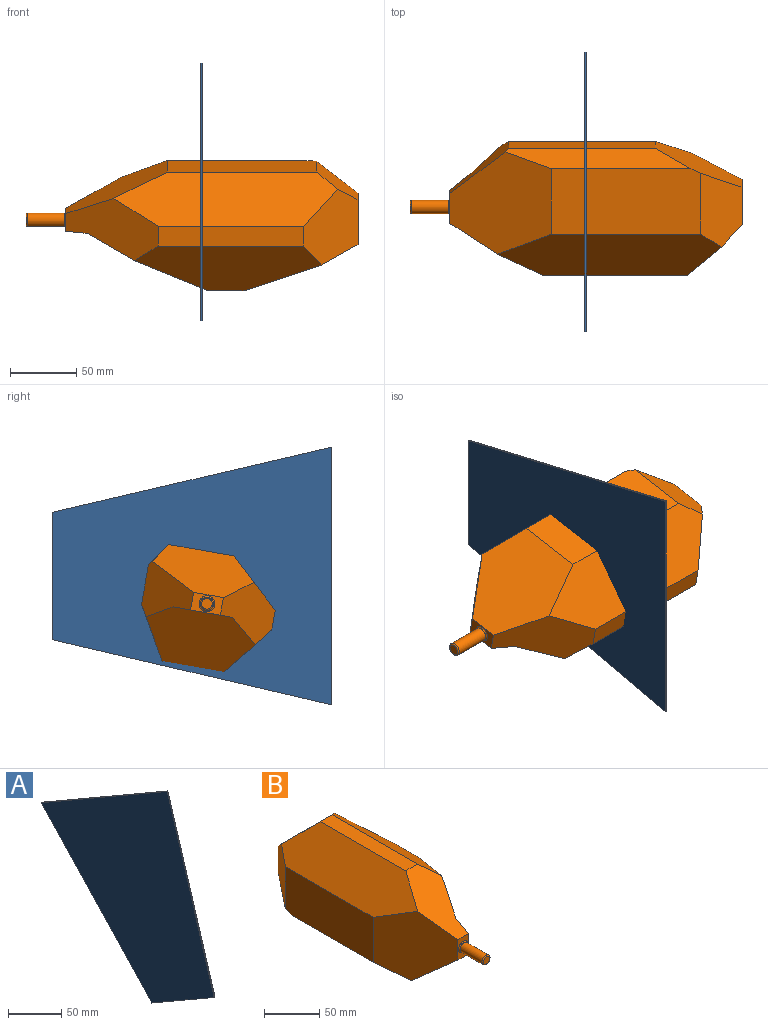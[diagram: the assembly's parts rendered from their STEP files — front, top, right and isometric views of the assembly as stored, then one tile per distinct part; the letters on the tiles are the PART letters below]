
ASSEMBLY  parts=2 mates=1
PART A: 6 faces, bbox 1x230.6x254.4 mm
  f0: plane 206.37x62.56mm, normal (0,-0.96,0.29), area 215.6mm2, adj f1,f3,f4,f5
  f1: plane 83.14x48mm, normal (0,-0.5,-0.87), area 96mm2, adj f0,f2,f4,f5
  f2: plane 157.37x147.44mm, normal (0,0.73,-0.68), area 215.6mm2, adj f1,f3,f4,f5
  f3: plane 168.01x97mm, normal (0,0.5,0.87), area 194mm2, adj f0,f2,f4,f5
  f4: plane 254.37x230.57mm, normal (1,0,0), area 30450mm2, adj f0,f1,f2,f3
  f5: plane 254.37x230.57mm, normal (-1,0,0), area 30450mm2, adj f0,f1,f2,f3
PART B: 27 faces, bbox 89.6x250x100 mm
  f0: plane 112.42x50mm, normal (-1,0,0), area 5608.5mm2, adj f1,f7,f10,f17,f18
  f1: plane 139.95x17.8mm, normal (-0.57,0,-0.82), area 2435.1mm2, adj f0,f2,f10,f11,f17
  f2: plane 110.51x30mm, normal (0,0,-1), area 3315.4mm2, adj f1,f3,f10,f11
  f3: plane 144.68x41.78mm, normal (0.5,0,-0.87), area 4745.3mm2, adj f2,f10,f11,f13,f15,f16
  f4: plane 34.32x28.5mm, normal (0,1,0), area 864.9mm2, adj f9,f10,f13,f18,f25
  f5: plane 140.88x39.58mm, normal (0.62,0,0.78), area 5073.2mm2, adj f6,f9,f12,f13,f15,f16
  f6: plane 109.36x15mm, normal (0,0,1), area 1640.4mm2, adj f5,f7,f9,f12
  f7: plane 168.48x37.49mm, normal (-0.73,0,0.68), area 7119.9mm2, adj f0,f6,f9,f12,f17,f18
  f8: plane 22.71x13.51mm, normal (0,-1,0), area 193.9mm2, adj f11,f12,f14,f17,f21
  f9: plane 55.91x41.08mm, normal (0,0.71,0.71), area 2322.1mm2, adj f4,f5,f6,f7,f13,f18
  f10: plane 70.66x65.24mm, normal (0,0.42,-0.91), area 3795.6mm2, adj f0,f1,f2,f3,f4,f13,f18
  f11: plane 44.25x41.86mm, normal (0,-0.64,-0.77), area 1519.5mm2, adj f1,f2,f3,f8,f14,f15,f17
  f12: plane 69.55x45.99mm, normal (0,-0.5,0.87), area 2221.4mm2, adj f5,f6,f7,f8,f14,f15,f17
  f13: plane 85.05x73.33mm, normal (0.93,0.37,0), area 5111mm2, adj f3,f4,f5,f9,f10,f16
  f14: plane 45.31x15.95mm, normal (1,0,0), area 542.6mm2, adj f8,f11,f12,f15
  f15: plane 90.59x84.59mm, normal (0.9,-0.44,0), area 6504.7mm2, adj f3,f5,f11,f12,f14,f16
  f16: plane 44.33x28.41mm, normal (1,0,0), area 1259.3mm2, adj f3,f5,f13,f15
  f17: plane 78.52x76.45mm, normal (-0.92,-0.39,0), area 4722.9mm2, adj f0,f1,f7,f8,f11,f12
  f18: plane 58.39x31.13mm, normal (-0.82,0.57,0), area 1683.7mm2, adj f0,f4,f7,f9,f10
  f19: cylinder r=5mm len=28mm, axis (0,1,0), area 879.6mm2, adj f21,f22
  f20: plane 8x8mm, normal (0,-1,0), area 50.3mm2, adj f22
  f21: torus R=6mm, axis (0,-1,0), area 52.9mm2, adj f8,f19
  f22: torus R=4mm, axis (0,-1,0), area 45.8mm2, adj f19,f20
  f23: cylinder r=5mm len=23mm, axis (0,1,0), area 722.6mm2, adj f25,f26
  f24: plane 8x8mm, normal (0,1,0), area 50.3mm2, adj f26
  f25: torus R=6mm, axis (0,-1,0), area 52.9mm2, adj f4,f23
  f26: torus R=4mm, axis (0,1,0), area 45.8mm2, adj f23,f24
PLACE A rot(axis=(1,0,0),120deg) t=(-69.28,153.34,77.47)mm
PLACE B rot(axis=(0.61,0.61,-0.51),125.9deg) t=(49.01,106.09,47.49)mm
MATE parallel B.f23 <-> A.f4  axis (1,0,0) through (49.01,114.48,45.02)mm
